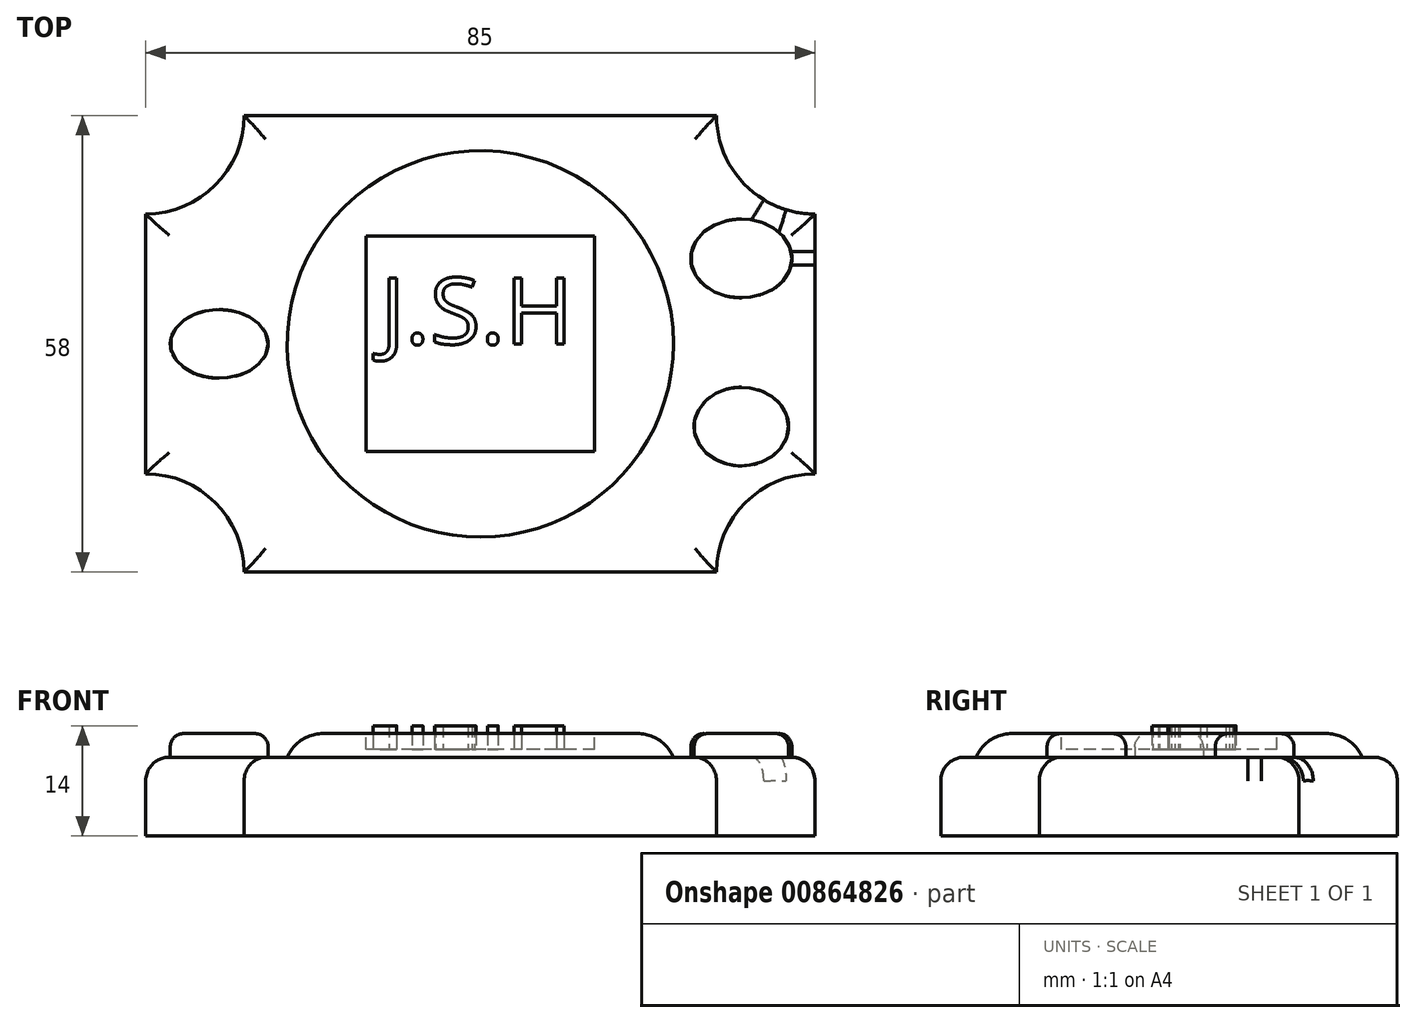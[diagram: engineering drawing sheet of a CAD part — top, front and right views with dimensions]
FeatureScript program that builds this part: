
annotation { "Feature Type Name" : "Feature", "Feature Type Description" : "" }
export const myFeature = defineFeature(function(context is Context, id is Id, definition is map)
    precondition{}
    {
        {
            var Q0;
            Q0=qCreatedBy(makeId("Top.planeOp"),FACE);
            var sketch = newSketch(context, id + "F0", { "sketchPlane" : qUnion([Q0])});
            skLineSegment(sketch, "E0.bottom", {"start": v(-30, 29) * mm, "end": v(30, 29) * mm});
            skLineSegment(sketch, "E0.top", {"start": v(-30, -29) * mm, "end": v(30, -29) * mm});
            skLineSegment(sketch, "E0.left", {"start": v(-42.5, 16.5) * mm, "end": v(-42.5, -16.5) * mm});
            skLineSegment(sketch, "E0.right", {"start": v(42.5, 16.5) * mm, "end": v(42.5, -16.5) * mm});
            skPoint(sketch, "E0.middle", {"position": v(0, 0) * mm});
            skArc(sketch, "E1", {"start": v(-42.5, 16.5) * mm, "mid": v(-33.66, 20.16) * mm, "end": v(-30, 29) * mm});
            skArc(sketch, "E2", {"start": v(30, 29) * mm, "mid": v(33.66, 20.16) * mm, "end": v(42.5, 16.5) * mm});
            skArc(sketch, "E3", {"start": v(-30, -29) * mm, "mid": v(-33.66, -20.16) * mm, "end": v(-42.5, -16.5) * mm});
            skArc(sketch, "E4", {"start": v(42.5, -16.5) * mm, "mid": v(33.66, -20.16) * mm, "end": v(30, -29) * mm});
            skSolve(sketch);
        }
        {
            var Q0;
            Q0=makeQuery(id+"F0.imprint","IMPRINT",FACE,{"disambiguationData":[TD([[makeQuery(id+"F0.imprint","IMPRINT",EDGE,{"derivedFrom":sQuery(id+"F0.wireOp",EDGE,"E0.bottom")}),-1.0]])]});
            extrude(context, id + "F1", {"entities" : qUnion([Q0]), "depth" : 10 * mm, "offsetDistance" : 25 * mm});
        }
        {
            var Q0;
            Q0=makeQuery(id+"F1.opExtrude","CAP_FACE",FACE,{"disambiguationData":[OSD([sQuery(id+"F0.wireOp",EDGE,"E0.bottom"),sQuery(id+"F0.wireOp",EDGE,"E0.top"),sQuery(id+"F0.wireOp",EDGE,"E0.left"),sQuery(id+"F0.wireOp",EDGE,"E0.right"),sQuery(id+"F0.wireOp",EDGE,"E1"),sQuery(id+"F0.wireOp",EDGE,"E2"),sQuery(id+"F0.wireOp",EDGE,"E3"),sQuery(id+"F0.wireOp",EDGE,"E4")])],"isStart":false});
            var sketch = newSketch(context, id + "F2", { "sketchPlane" : qUnion([Q0])});
            skCircle(sketch, "E5", {"center": v(0, 0) * mm, "radius": 19.54 * mm});
            skLineSegment(sketch, "E6.0", {"start": v(13.81, 13.81) * mm, "end": v(13.81, -13.81) * mm});
            skLineSegment(sketch, "E6.1", {"start": v(13.81, -13.81) * mm, "end": v(-13.81, -13.81) * mm});
            skLineSegment(sketch, "E6.2", {"start": v(-13.81, -13.81) * mm, "end": v(-13.81, 13.81) * mm});
            skLineSegment(sketch, "E6.3", {"start": v(-13.81, 13.81) * mm, "end": v(13.81, 13.81) * mm});
            skCircle(sketch, "E7.0", {"center": v(0, 0) * mm, "radius": 24.54 * mm});
            skSolve(sketch);
        }
        {
            var Q0;
            Q0 = qSketchRegion(id + "F2", true);
            extrude(context, id + "F3", {"entities" : qUnion([Q0]), "operationType" : NewBodyOperationType.ADD, "depth" : 3 * mm, "offsetDistance" : 25 * mm});
        }
        {
            var Q0;
            Q0=makeQuery(id+"F3.boolean.opBoolean","SPLIT",FACE,{"disambiguationData":[TD([makeQuery(id+"F3.opExtrude","SWEPT_FACE",FACE,{"disambiguationData":[OSD([sQuery(id+"F2.wireOp",EDGE,"E5")])]})])],"derivedFrom":makeQuery(id+"F1.opExtrude","CAP_FACE",FACE,{"disambiguationData":[OSD([sQuery(id+"F0.wireOp",EDGE,"E0.bottom"),sQuery(id+"F0.wireOp",EDGE,"E0.top"),sQuery(id+"F0.wireOp",EDGE,"E0.left"),sQuery(id+"F0.wireOp",EDGE,"E0.right"),sQuery(id+"F0.wireOp",EDGE,"E1"),sQuery(id+"F0.wireOp",EDGE,"E2"),sQuery(id+"F0.wireOp",EDGE,"E3"),sQuery(id+"F0.wireOp",EDGE,"E4")])],"isStart":false})});
            extrude(context, id + "F4", {"entities" : qUnion([Q0]), "operationType" : NewBodyOperationType.ADD, "depth" : 3 * mm, "offsetDistance" : 25 * mm});
        }
        {
            var Q0;
            Q0=makeQuery(id+"F3.opExtrude","CAP_EDGE",EDGE,{"disambiguationData":[OSD([sQuery(id+"F2.wireOp",EDGE,"E7.0")])],"isStart":false});
            fillet(context, id + "F5", {"entities" : qUnion([Q0]), "radius" : 5 * mm, "tangentPropagation" : true, "allowEdgeOverflow" : false});
        }
        {
            var Q0;
            Q0=makeQuery(id+"F4.boolean.opBoolean","MERGE",FACE,{"derivedFrom":[makeQuery(id+"F3.opExtrude","CAP_FACE",FACE,{"disambiguationData":[OSD([sQuery(id+"F2.wireOp",EDGE,"E5"),sQuery(id+"F2.wireOp",EDGE,"E7.0")])],"isStart":false}),makeQuery(id+"F4.opExtrude","CAP_FACE",FACE,{"disambiguationData":[OSD([sQuery(id+"F0.wireOp",EDGE,"E0.bottom"),sQuery(id+"F0.wireOp",EDGE,"E0.top"),sQuery(id+"F0.wireOp",EDGE,"E0.left"),sQuery(id+"F0.wireOp",EDGE,"E0.right"),sQuery(id+"F0.wireOp",EDGE,"E1"),sQuery(id+"F0.wireOp",EDGE,"E2"),sQuery(id+"F0.wireOp",EDGE,"E3"),sQuery(id+"F0.wireOp",EDGE,"E4")])],"isStart":false})]});
            var sketch = newSketch(context, id + "F6", { "sketchPlane" : qUnion([Q0])});
            skLineSegment(sketch, "E8.bottom", {"start": v(14.52, 13.68) * mm, "end": v(-14.52, 13.68) * mm});
            skLineSegment(sketch, "E8.top", {"start": v(14.52, -13.68) * mm, "end": v(-14.52, -13.68) * mm});
            skLineSegment(sketch, "E8.left", {"start": v(14.52, 13.68) * mm, "end": v(14.52, -13.68) * mm});
            skLineSegment(sketch, "E8.right", {"start": v(-14.52, 13.68) * mm, "end": v(-14.52, -13.68) * mm});
            skPoint(sketch, "E8.middle", {"position": v(0, 0) * mm});
            skSolve(sketch);
        }
        {
            var Q0;
            Q0=makeQuery(id+"F6.imprint","IMPRINT",FACE,{"disambiguationData":[TD([[makeQuery(id+"F6.imprint","IMPRINT",EDGE,{"derivedFrom":sQuery(id+"F6.wireOp",EDGE,"E8.bottom")}),1.0]])]});
            extrude(context, id + "F7", {"entities" : qUnion([Q0]), "operationType" : NewBodyOperationType.REMOVE, "oppositeDirection" : true, "depth" : 2 * mm, "offsetDistance" : 25 * mm});
        }
        {
            var Q0;
            {var subQ0=sQuery(id+"F0.wireOp",EDGE,"E0.left");var subQ1=sQuery(id+"F0.wireOp",EDGE,"E0.top");var subQ2=sQuery(id+"F0.wireOp",EDGE,"E0.right");var subQ3=sQuery(id+"F0.wireOp",EDGE,"E0.bottom");var subQ4=sQuery(id+"F0.wireOp",EDGE,"E1");var subQ5=sQuery(id+"F0.wireOp",EDGE,"E2");var subQ6=sQuery(id+"F0.wireOp",EDGE,"E3");var subQ7=sQuery(id+"F0.wireOp",EDGE,"E4");Q0=makeQuery(id+"F3.boolean.opBoolean","SPLIT",FACE,{"disambiguationData":[TD([makeQuery(id+"F1.opExtrude","SWEPT_FACE",FACE,{"disambiguationData":[OSD([subQ3])]})])],"derivedFrom":makeQuery(id+"F1.opExtrude","CAP_FACE",FACE,{"disambiguationData":[OSD([subQ3,subQ1,subQ0,subQ2,subQ4,subQ5,subQ6,subQ7])],"isStart":false})});}
            var sketch = newSketch(context, id + "F8", { "sketchPlane" : qUnion([Q0])});
            skEllipse(sketch, "E9", {"center": v(-33.16, 0) * mm, "majorRadius": 6.21 * mm, "minorRadius": 4.35 * mm, "majorAxis": v(1, 0)});
            skEllipse(sketch, "E10", {"center": v(33.16, 10.85) * mm, "majorRadius": 6.43 * mm, "minorRadius": 5 * mm, "majorAxis": v(1, 0)});
            skEllipse(sketch, "E11", {"center": v(33.16, -10.5) * mm, "majorRadius": 6 * mm, "minorRadius": 5 * mm, "majorAxis": v(1, 0)});
            skSolve(sketch);
        }
        {
            var Q0;
            Q0=makeQuery(id+"F8.imprint","IMPRINT",FACE,{"disambiguationData":[TD([[makeQuery(id+"F8.imprint","IMPRINT",EDGE,{"derivedFrom":sQuery(id+"F8.wireOp",EDGE,"E9")}),1.0]])]});
            var Q1;
            Q1=makeQuery(id+"F8.imprint","IMPRINT",FACE,{"disambiguationData":[TD([[makeQuery(id+"F8.imprint","IMPRINT",EDGE,{"derivedFrom":sQuery(id+"F8.wireOp",EDGE,"E10")}),1.0]])]});
            var Q2;
            Q2=makeQuery(id+"F8.imprint","IMPRINT",FACE,{"disambiguationData":[TD([[makeQuery(id+"F8.imprint","IMPRINT",EDGE,{"derivedFrom":sQuery(id+"F8.wireOp",EDGE,"E11")}),1.0]])]});
            extrude(context, id + "F9", {"entities" : qUnion([Q0, Q1, Q2]), "operationType" : NewBodyOperationType.ADD, "depth" : 3 * mm, "offsetDistance" : 25 * mm});
        }
        {
            var Q0;
            Q0=makeQuery(id+"F9.opExtrude","CAP_FACE",FACE,{"disambiguationData":[OSD([sQuery(id+"F8.wireOp",EDGE,"E9")])],"isStart":false});
            fillet(context, id + "F10", {"entities" : qUnion([Q0]), "radius" : 1.69 * mm, "tangentPropagation" : true, "allowEdgeOverflow" : false});
        }
        {
            var Q0;
            Q0=makeQuery(id+"F9.opExtrude","CAP_FACE",FACE,{"disambiguationData":[OSD([sQuery(id+"F8.wireOp",EDGE,"E10")])],"isStart":false});
            var Q1;
            Q1=makeQuery(id+"F9.opExtrude","CAP_FACE",FACE,{"disambiguationData":[OSD([sQuery(id+"F8.wireOp",EDGE,"E11")])],"isStart":false});
            fillet(context, id + "F11", {"entities" : qUnion([Q0, Q1]), "radius" : 1.69 * mm, "tangentPropagation" : true, "allowEdgeOverflow" : false});
        }
        {
            var Q0;
            Q0=makeQuery(id+"F7.boolean.opBoolean","COPY",FACE,{"derivedFrom":makeQuery(id+"F7.opExtrude","CAP_FACE",FACE,{"disambiguationData":[OSD([sQuery(id+"F6.wireOp",EDGE,"E8.bottom"),sQuery(id+"F6.wireOp",EDGE,"E8.top"),sQuery(id+"F6.wireOp",EDGE,"E8.left"),sQuery(id+"F6.wireOp",EDGE,"E8.right")])],"isStart":false})});
            var sketch = newSketch(context, id + "F12", { "sketchPlane" : qUnion([Q0])});
            skPoint(sketch, "E12.secondSnap0", {"position": v(14.52, 0) * mm});
            skText(sketch, "E13", { "text": "J.S.H", "fontName": "OpenSans-Regular.ttf"});
            const initialGuessF12  = {"E13": [-0.01268, 0, 1, 0, 0.00845]};
            skSetInitialGuess(sketch, initialGuessF12);
            skSolve(sketch);
        }
        {
            var Q0;
            Q0 = qSketchRegion(id + "F12", true);
            extrude(context, id + "F13", {"entities" : qUnion([Q0]), "operationType" : NewBodyOperationType.ADD, "depth" : 3 * mm, "offsetDistance" : 25 * mm});
        }
        {
            var Q0;
            Q0=makeQuery(id+"F1.opExtrude","CAP_EDGE",EDGE,{"disambiguationData":[OSD([sQuery(id+"F0.wireOp",EDGE,"E0.bottom")])],"isStart":false});
            var Q1;
            Q1=makeQuery(id+"F1.opExtrude","CAP_EDGE",EDGE,{"disambiguationData":[OSD([sQuery(id+"F0.wireOp",EDGE,"E1")])],"isStart":false});
            var Q2;
            Q2=makeQuery(id+"F1.opExtrude","CAP_EDGE",EDGE,{"disambiguationData":[OSD([sQuery(id+"F0.wireOp",EDGE,"E0.left")])],"isStart":false});
            var Q3;
            Q3=makeQuery(id+"F1.opExtrude","CAP_EDGE",EDGE,{"disambiguationData":[OSD([sQuery(id+"F0.wireOp",EDGE,"E3")])],"isStart":false});
            var Q4;
            Q4=makeQuery(id+"F1.opExtrude","CAP_EDGE",EDGE,{"disambiguationData":[OSD([sQuery(id+"F0.wireOp",EDGE,"E0.top")])],"isStart":false});
            var Q5;
            Q5=makeQuery(id+"F1.opExtrude","CAP_EDGE",EDGE,{"disambiguationData":[OSD([sQuery(id+"F0.wireOp",EDGE,"E4")])],"isStart":false});
            var Q6;
            Q6=makeQuery(id+"F1.opExtrude","CAP_EDGE",EDGE,{"disambiguationData":[OSD([sQuery(id+"F0.wireOp",EDGE,"E0.right")])],"isStart":false});
            var Q7;
            Q7=makeQuery(id+"F1.opExtrude","CAP_EDGE",EDGE,{"disambiguationData":[OSD([sQuery(id+"F0.wireOp",EDGE,"E2")])],"isStart":false});
            fillet(context, id + "F14", {"entities" : qUnion([Q0, Q1, Q2, Q3, Q4, Q5, Q6, Q7]), "radius" : 3 * mm, "tangentPropagation" : true, "allowEdgeOverflow" : false});
        }
    });
